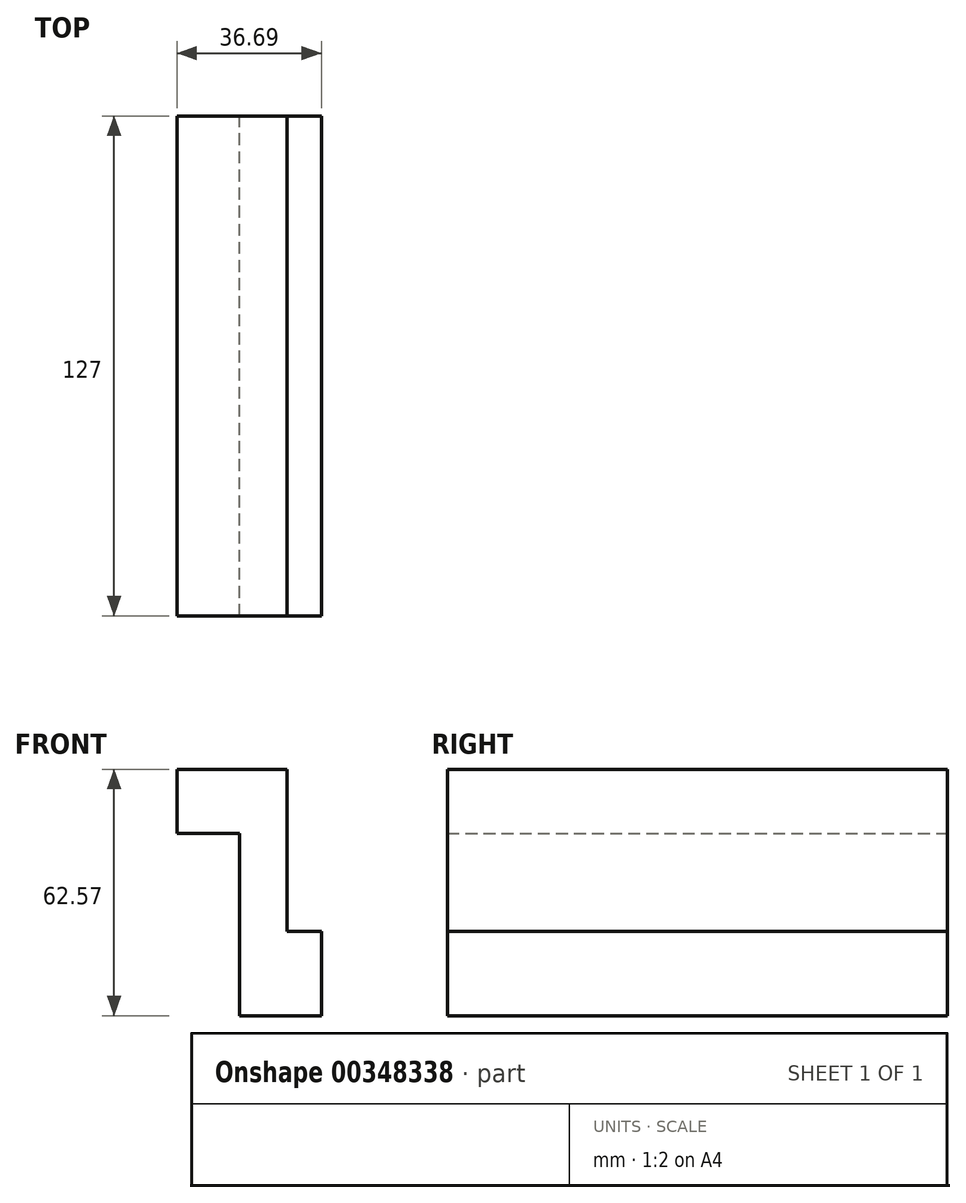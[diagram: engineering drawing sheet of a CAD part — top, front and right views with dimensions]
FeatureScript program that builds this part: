
annotation { "Feature Type Name" : "Feature", "Feature Type Description" : "" }
export const myFeature = defineFeature(function(context is Context, id is Id, definition is map)
    precondition{}
    {
        {
            var Q0;
            Q0=qCreatedBy(makeId("Front.planeOp"),FACE);
            var sketch = newSketch(context, id + "F0", { "sketchPlane" : qUnion([Q0])});
            skLineSegment(sketch, "E0", {"start": v(0, 0) * mm, "end": v(0, 41.2) * mm});
            skLineSegment(sketch, "E1", {"start": v(0, 41.2) * mm, "end": v(-27.97, 41.2) * mm});
            skLineSegment(sketch, "E2", {"start": v(-27.97, 41.2) * mm, "end": v(-27.97, 24.97) * mm});
            skLineSegment(sketch, "E3", {"start": v(-27.97, 24.97) * mm, "end": v(-12.03, 24.97) * mm});
            skLineSegment(sketch, "E4", {"start": v(-12.03, 24.97) * mm, "end": v(-12.03, 11.43) * mm});
            skLineSegment(sketch, "E5", {"start": v(-12.03, 11.43) * mm, "end": v(-12.03, -21.36) * mm});
            skLineSegment(sketch, "E6", {"start": v(-12.03, -21.36) * mm, "end": v(8.72, -21.36) * mm});
            skLineSegment(sketch, "E7", {"start": v(8.72, -21.36) * mm, "end": v(8.72, 0) * mm});
            skLineSegment(sketch, "E8", {"start": v(8.72, 0) * mm, "end": v(0, 0) * mm});
            skSolve(sketch);
        }
        {
            var Q0;
            Q0=makeQuery(id+"F0.imprint","IMPRINT",FACE,{"disambiguationData":[TD([[makeQuery(id+"F0.imprint","IMPRINT",EDGE,{"derivedFrom":sQuery(id+"F0.wireOp",EDGE,"E0")}),1.0]])]});
            extrude(context, id + "F1", {"entities" : qUnion([Q0]), "depth" : 127 * mm});
        }
    });
